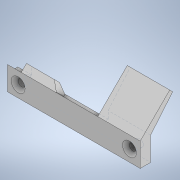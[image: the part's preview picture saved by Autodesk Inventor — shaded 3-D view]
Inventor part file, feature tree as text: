
AUTODESK INVENTOR PART (.ipt)
format: ipt  version: 2021 (Build 250183000, 183)  size: 166,912 bytes
history: native  units: mm
features: sketch x5, extrude x4, hole x1, chamfer x1
ambient origin geometry x8: Origin, YZ Plane, XZ Plane, XY Plane, X Axis, Y Axis, Z Axis, Center Point
bodies: Solid1 (feature_tree)
feature tree (11):
  extrude  "Extrusion1"  Depth=38.2mm
  hole  "Hole1"  [1 undecoded]
  extrude  "Extrusion2"  Depth=3.0mm
  extrude  "Extrusion3"  Depth=32.0mm
  extrude  "Extrusion4"  Depth=0.88mm
  chamfer  "Chamfer1"  Distance=12.0mm
  sketch  "Sketch1"  dims[d0=38.2mm d1=6.8mm]
  sketch  "Sketch2"  dims[d2=19.1mm d3=3.4mm]
  sketch  "Sketch3"  dims[d4=3.0mm d5=0.0mm d6=3.5mm]
  sketch  "Sketch4"  dims[d7=3.5mm d8=32.0mm]
  sketch  "Sketch5"  dims[d9=3.1mm d10=3.1mm d11=2.0mm d12=6.0mm d13=4.0mm d14=2.0mm d15=90.0deg d16=4.0mm d17=20.594885mm d18=12.0mm d19=45.0deg d20=1.2mm d21=38.2mm d22=0.0mm d23=4.0mm d24=4.0mm d25=14.0mm d26=26.0mm d27=3.0mm d28=0.0mm d29=0.88mm d30=0.0mm d31=2.0mm d32=2.0mm d33=45.0deg]
note: 1 required parameter value undecoded (feature->parameter linkage not recoverable at this tier; creation-order binding heuristic only, values carry confidence <= 0.55)
